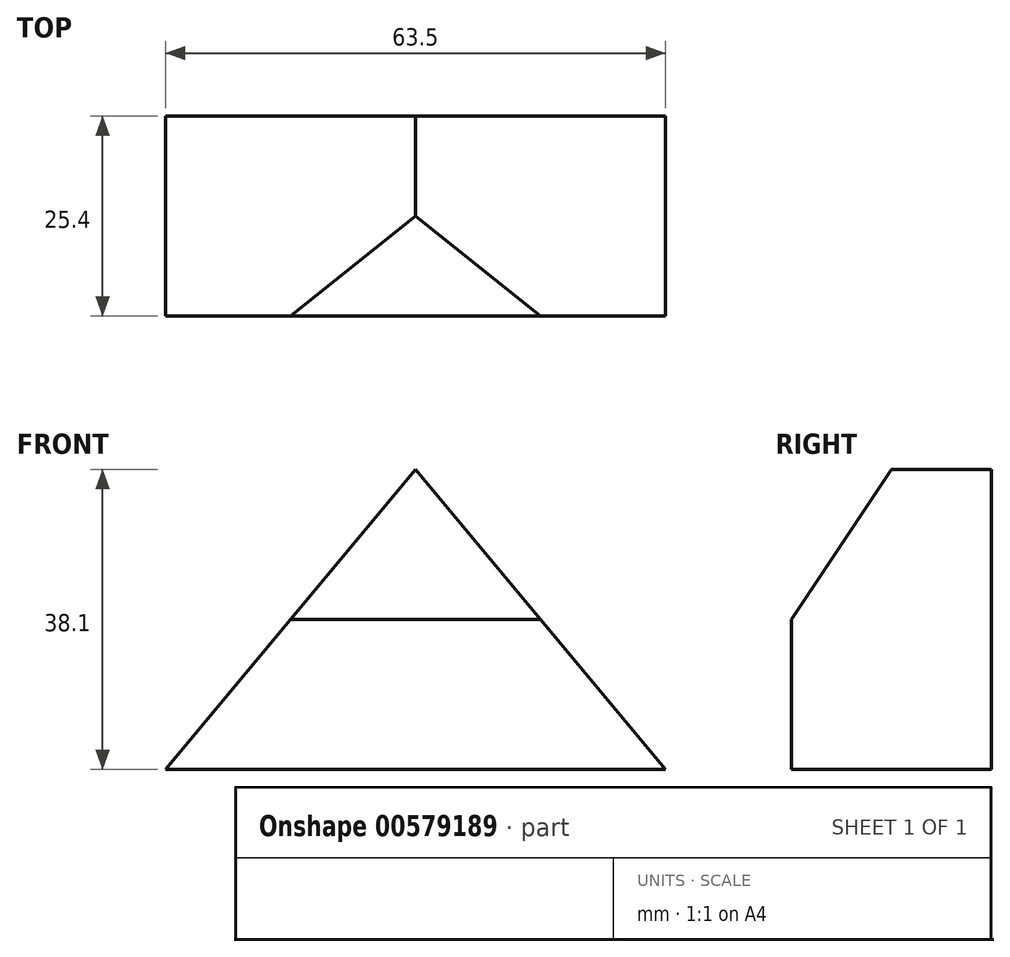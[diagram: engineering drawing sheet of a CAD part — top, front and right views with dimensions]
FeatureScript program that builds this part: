
annotation { "Feature Type Name" : "Feature", "Feature Type Description" : "" }
export const myFeature = defineFeature(function(context is Context, id is Id, definition is map)
    precondition{}
    {
        {
            var Q0;
            Q0=qCreatedBy(makeId("Front.planeOp"),FACE);
            var sketch = newSketch(context, id + "F0", { "sketchPlane" : qUnion([Q0])});
            skLineSegment(sketch, "E0.top", {"start": v(0, 0) * mm, "end": v(63.5, 0) * mm});
            skLineSegment(sketch, "E1", {"start": v(15.88, 19.05) * mm, "end": v(47.62, 19.05) * mm});
            skLineSegment(sketch, "E2", {"start": v(0, 0) * mm, "end": v(15.88, 19.05) * mm});
            skLineSegment(sketch, "E3", {"start": v(31.75, 38.1) * mm, "end": v(47.62, 19.05) * mm});
            skLineSegment(sketch, "E4", {"start": v(15.88, 19.05) * mm, "end": v(31.75, 38.1) * mm});
            skLineSegment(sketch, "E5", {"start": v(47.62, 19.05) * mm, "end": v(63.5, 0) * mm});
            skPoint(sketch, "E6.orphan", {"position": v(0, 38.1) * mm});
            skPoint(sketch, "E7.orphan", {"position": v(63.5, 38.1) * mm});
            skPoint(sketch, "E0.right.start.orphan", {"position": v(63.5, 19.05) * mm});
            skPoint(sketch, "E0.left.start.orphan", {"position": v(0, 19.05) * mm});
            skSolve(sketch);
        }
        {
            var Q0;
            Q0=makeQuery(id+"F0.imprint","IMPRINT",FACE,{"disambiguationData":[TD([[makeQuery(id+"F0.imprint","IMPRINT",EDGE,{"derivedFrom":sQuery(id+"F0.wireOp",EDGE,"E0.top")}),1.0]])]});
            extrude(context, id + "F1", {"entities" : qUnion([Q0]), "depth" : 25.4 * mm, "offsetDistance" : 25.4 * mm});
        }
        {
            var Q0;
            Q0 = qSketchRegion(id + "F0", true);
            extrude(context, id + "F2", {"entities" : qUnion([Q0]), "operationType" : NewBodyOperationType.ADD, "depth" : 25.4 * mm, "offsetDistance" : 25.4 * mm});
        }
        {
            var Q0;
            Q0=makeQuery(id+"F1.opExtrude","CAP_EDGE",EDGE,{"disambiguationData":[OSD([sQuery(id+"F0.wireOp",EDGE,"E0.top")])],"isStart":false});
            cPoint(context, id + "F3", {"entities" : qUnion([Q0]), "parameter" : 0.5});
        }
        {
            var Q0;
            Q0=makeQuery(id+"F2.opExtrude","CAP_VERTEX",VERTEX,{"disambiguationData":[OSD([sQuery(id+"F0.wireOp",EDGE,"E3"),sQuery(id+"F0.wireOp",EDGE,"E4")])],"isStart":false});
            var Q1;
            Q1=makeQuery(id+"F2.opExtrude","CAP_VERTEX",VERTEX,{"disambiguationData":[OSD([sQuery(id+"F0.wireOp",EDGE,"E3"),sQuery(id+"F0.wireOp",EDGE,"E4")])],"isStart":true});
            var Q2;
            Q2 = qCreatedBy(id + "F3" ,VERTEX);
            cPlane(context, id + "F4", {"entities" : qUnion([Q0, Q1, Q2]), "cplaneType" : CPlaneType.THREE_POINT, "offset" : 25.4 * mm, "width" : 152.4 * mm, "height" : 152.4 * mm});
        }
        {
            var Q0;
            Q0=qCreatedBy(id+"F4.planeOp",FACE);
            var sketch = newSketch(context, id + "F5", { "sketchPlane" : qUnion([Q0])});
            skLineSegment(sketch, "E8", {"start": v(-12.7, 38.1) * mm, "end": v(-25.4, 38.1) * mm});
            skLineSegment(sketch, "E9", {"start": v(-25.4, 38.1) * mm, "end": v(-25.4, 19.05) * mm});
            skLineSegment(sketch, "E10", {"start": v(-25.4, 19.05) * mm, "end": v(-12.7, 38.1) * mm});
            skSolve(sketch);
        }
        {
            var Q0;
            Q0 = qSketchRegion(id + "F5", true);
            extrude(context, id + "F6", {"entities" : qUnion([Q0]), "operationType" : NewBodyOperationType.REMOVE, "endBound" : BoundingType.SYMMETRIC, "depth" : 31.75 * mm, "offsetDistance" : 25.4 * mm});
        }
    });
